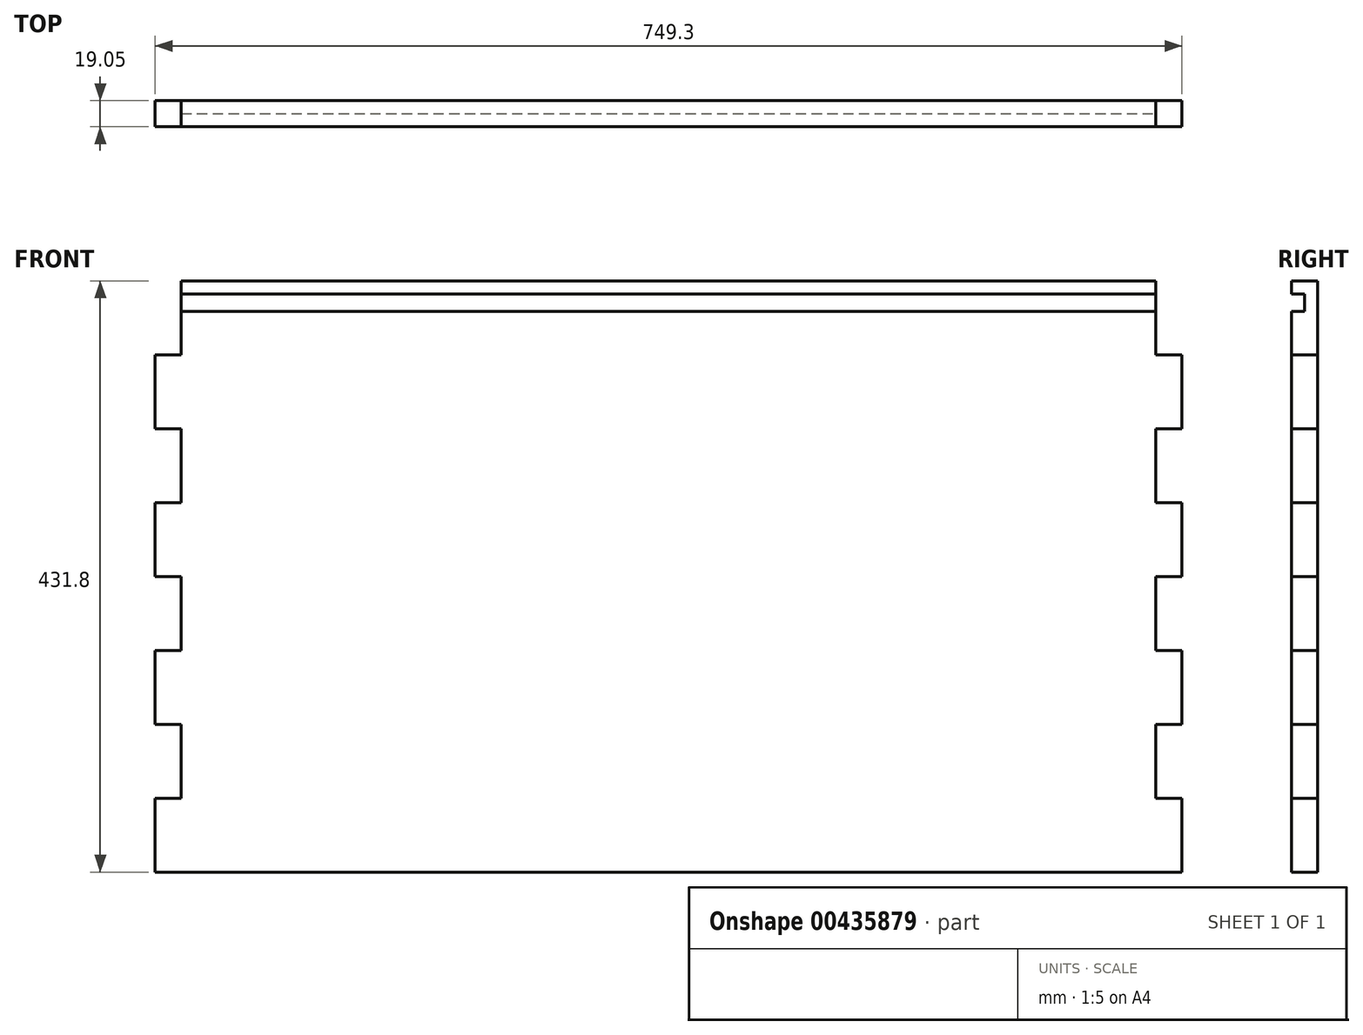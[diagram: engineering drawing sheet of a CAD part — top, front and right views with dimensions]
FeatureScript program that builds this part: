
annotation { "Feature Type Name" : "Feature", "Feature Type Description" : "" }
export const myFeature = defineFeature(function(context is Context, id is Id, definition is map)
    precondition{}
    {
        {
            var Q0;
            Q0=qCreatedBy(makeId("Front.planeOp"),FACE);
            var sketch = newSketch(context, id + "F0", { "sketchPlane" : qUnion([Q0])});
            skLineSegment(sketch, "E0.bottom", {"start": v(0, 0) * mm, "end": v(749.3, 0) * mm});
            skLineSegment(sketch, "E0.top", {"start": v(19.05, 431.8) * mm, "end": v(730.25, 431.8) * mm});
            skLineSegment(sketch, "E1", {"start": v(0, 0) * mm, "end": v(0, 53.98) * mm});
            skLineSegment(sketch, "E2", {"start": v(0, 53.98) * mm, "end": v(19.05, 53.98) * mm});
            skLineSegment(sketch, "E3", {"start": v(19.05, 53.98) * mm, "end": v(19.05, 107.95) * mm});
            skLineSegment(sketch, "E4", {"start": v(19.05, 107.95) * mm, "end": v(0, 107.95) * mm});
            skLineSegment(sketch, "E5", {"start": v(0, 107.95) * mm, "end": v(0, 161.93) * mm});
            skLineSegment(sketch, "E6", {"start": v(0, 161.93) * mm, "end": v(19.05, 161.93) * mm});
            skLineSegment(sketch, "E7", {"start": v(19.05, 161.93) * mm, "end": v(19.05, 215.9) * mm});
            skLineSegment(sketch, "E8", {"start": v(19.05, 215.9) * mm, "end": v(0, 215.9) * mm});
            skLineSegment(sketch, "E9", {"start": v(0, 215.9) * mm, "end": v(0, 269.88) * mm});
            skLineSegment(sketch, "E10", {"start": v(0, 269.88) * mm, "end": v(19.05, 269.88) * mm});
            skLineSegment(sketch, "E11", {"start": v(19.05, 269.88) * mm, "end": v(19.05, 323.85) * mm});
            skLineSegment(sketch, "E12", {"start": v(19.05, 323.85) * mm, "end": v(0, 323.85) * mm});
            skLineSegment(sketch, "E13", {"start": v(0, 323.85) * mm, "end": v(0, 377.83) * mm});
            skLineSegment(sketch, "E14", {"start": v(0, 377.83) * mm, "end": v(19.05, 377.83) * mm});
            skLineSegment(sketch, "E15", {"start": v(19.05, 377.83) * mm, "end": v(19.05, 431.8) * mm});
            skLineSegment(sketch, "E16", {"start": v(749.3, 0) * mm, "end": v(749.3, 53.98) * mm});
            skLineSegment(sketch, "E17", {"start": v(749.3, 53.98) * mm, "end": v(730.25, 53.98) * mm});
            skLineSegment(sketch, "E18", {"start": v(730.25, 53.98) * mm, "end": v(730.25, 107.95) * mm});
            skLineSegment(sketch, "E19", {"start": v(730.25, 107.95) * mm, "end": v(749.3, 107.95) * mm});
            skLineSegment(sketch, "E20", {"start": v(749.3, 107.95) * mm, "end": v(749.3, 161.93) * mm});
            skLineSegment(sketch, "E21", {"start": v(749.3, 161.93) * mm, "end": v(730.25, 161.93) * mm});
            skLineSegment(sketch, "E22", {"start": v(730.25, 161.93) * mm, "end": v(730.25, 215.9) * mm});
            skLineSegment(sketch, "E23", {"start": v(730.25, 215.9) * mm, "end": v(749.3, 215.9) * mm});
            skLineSegment(sketch, "E24", {"start": v(749.3, 215.9) * mm, "end": v(749.3, 269.88) * mm});
            skLineSegment(sketch, "E25", {"start": v(749.3, 269.88) * mm, "end": v(730.25, 269.88) * mm});
            skLineSegment(sketch, "E26", {"start": v(730.25, 269.88) * mm, "end": v(730.25, 323.85) * mm});
            skLineSegment(sketch, "E27", {"start": v(730.25, 323.85) * mm, "end": v(749.3, 323.85) * mm});
            skLineSegment(sketch, "E28", {"start": v(749.3, 323.85) * mm, "end": v(749.3, 377.83) * mm});
            skLineSegment(sketch, "E29", {"start": v(749.3, 377.83) * mm, "end": v(730.25, 377.83) * mm});
            skLineSegment(sketch, "E30", {"start": v(730.25, 377.83) * mm, "end": v(730.25, 431.8) * mm});
            skSolve(sketch);
        }
        {
            var Q0;
            Q0=makeQuery(id+"F0.imprint","IMPRINT",FACE,{"disambiguationData":[TD([[makeQuery(id+"F0.imprint","IMPRINT",EDGE,{"derivedFrom":sQuery(id+"F0.wireOp",EDGE,"E0.bottom")}),1.0]])]});
            extrude(context, id + "F1", {"entities" : qUnion([Q0]), "depth" : 19.05 * mm});
        }
        {
            var Q0;
            Q0=makeQuery(id+"F1.opExtrude","SWEPT_FACE",FACE,{"disambiguationData":[OSD([sQuery(id+"F0.wireOp",EDGE,"E30")])]});
            var sketch = newSketch(context, id + "F2", { "sketchPlane" : qUnion([Q0])});
            skLineSegment(sketch, "E31", {"start": v(-19.05, 422.28) * mm, "end": v(-9.53, 422.28) * mm});
            skLineSegment(sketch, "E32", {"start": v(-9.53, 422.28) * mm, "end": v(-9.53, 409.58) * mm});
            skLineSegment(sketch, "E33", {"start": v(-9.53, 409.58) * mm, "end": v(-19.05, 409.58) * mm});
            skSolve(sketch);
        }
        {
            var Q0;
            {var subQ0=sQuery(id+"F2.wireOp",EDGE,"E31");Q0=makeQuery(id+"F2.imprint","IMPRINT",FACE,{"disambiguationData":[TD([[makeQuery(id+"F2.imprint","IMPRINT",EDGE,{"derivedFrom":subQ0}),-1.0]])]});}
            extrude(context, id + "F3", {"entities" : qUnion([Q0]), "operationType" : NewBodyOperationType.REMOVE, "endBound" : BoundingType.THROUGH_ALL, "oppositeDirection" : true, "depth" : 25.4 * mm});
        }
    });
